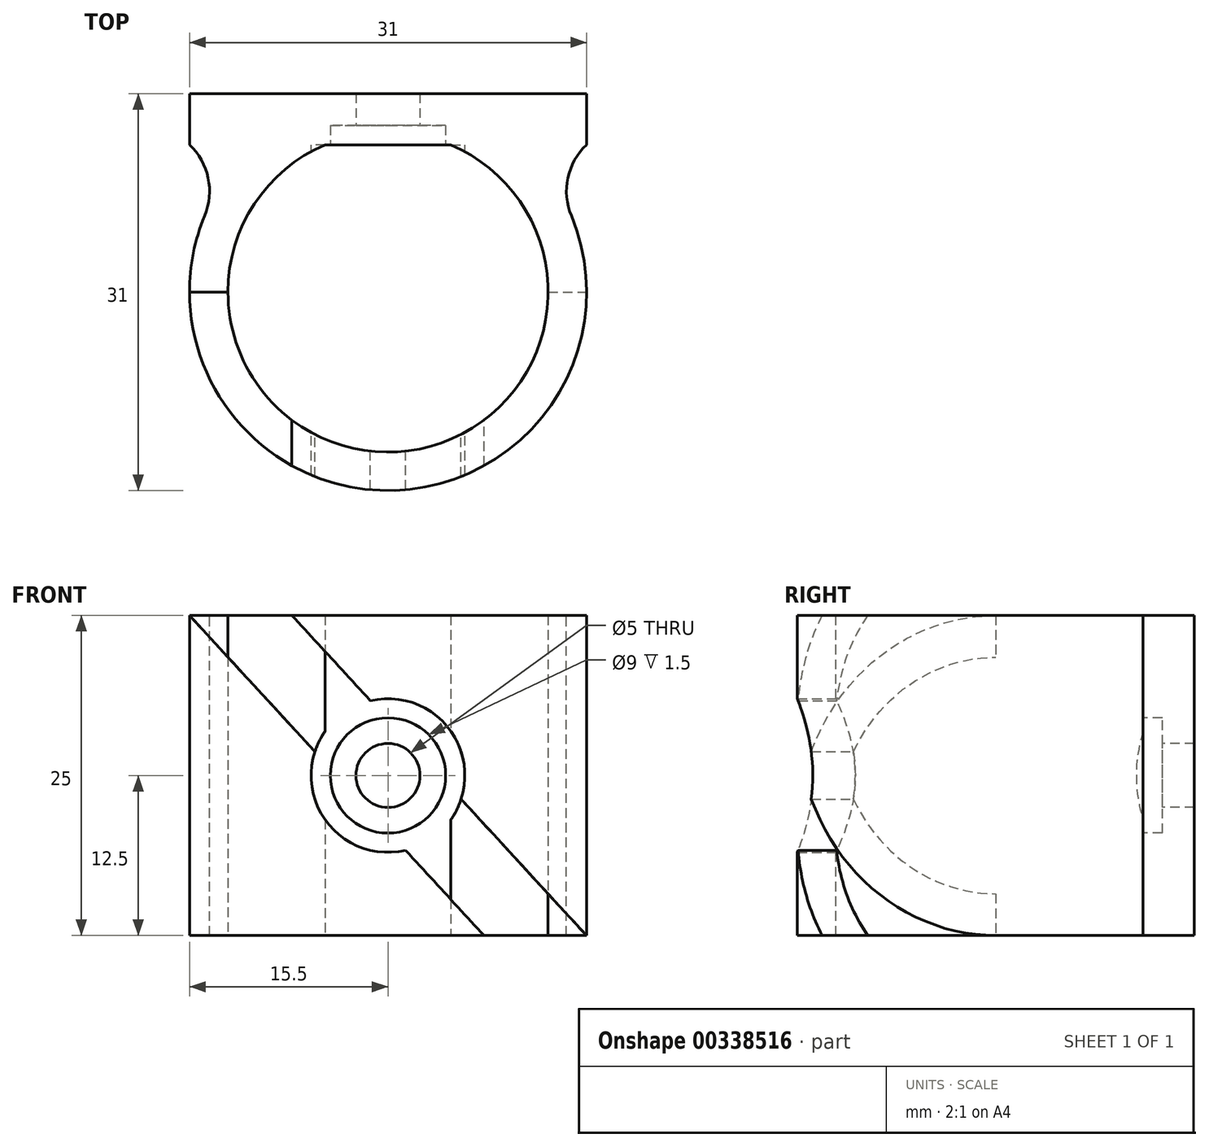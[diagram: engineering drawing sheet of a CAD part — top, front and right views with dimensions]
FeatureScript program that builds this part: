
annotation { "Feature Type Name" : "Feature", "Feature Type Description" : "" }
export const myFeature = defineFeature(function(context is Context, id is Id, definition is map)
    precondition{}
    {
        {
            var Q0;
            Q0=qCreatedBy(makeId("Top.planeOp"),FACE);
            var sketch = newSketch(context, id + "F0", { "sketchPlane" : qUnion([Q0])});
            skArc(sketch, "E0", {"start": v(-4.9, 11.5) * mm, "mid": v(0, -12.5) * mm, "end": v(4.9, 11.5) * mm});
            skArc(sketch, "E1.0", {"start": v(-10.4, 11.5) * mm, "mid": v(0, -15.5) * mm, "end": v(10.4, 11.5) * mm});
            skLineSegment(sketch, "E2.bottom", {"start": v(-15.5, 15.5) * mm, "end": v(15.5, 15.5) * mm});
            skLineSegment(sketch, "E2.top", {"start": v(-15.5, 11.5) * mm, "end": v(15.5, 11.5) * mm});
            skLineSegment(sketch, "E2.left", {"start": v(-15.5, 15.5) * mm, "end": v(-15.5, 11.5) * mm});
            skLineSegment(sketch, "E2.right", {"start": v(15.5, 15.5) * mm, "end": v(15.5, 11.5) * mm});
            skSolve(sketch);
        }
        {
            var Q0;
            {var subQ0=sQuery(id+"F0.wireOp",EDGE,"E0");Q0=makeQuery(id+"F0.imprint","IMPRINT",FACE,{"disambiguationData":[TD([[makeQuery(id+"F0.imprint","IMPRINT",EDGE,{"derivedFrom":subQ0}),-1.0]])]});}
            var Q1;
            Q1=makeQuery(id+"F0.imprint","IMPRINT",FACE,{"disambiguationData":[TD([[makeQuery(id+"F0.imprint","IMPRINT",EDGE,{"derivedFrom":sQuery(id+"F0.wireOp",EDGE,"E2.bottom")}),-1.0]])]});
            extrude(context, id + "F1", {"entities" : qUnion([Q0, Q1]), "depth" : 25 * mm, "offsetDistance" : 25 * mm});
        }
        {
            var Q0;
            {var subQ0=sQuery(id+"F0.wireOp",EDGE,"E2.top");var subQ1=sQuery(id+"F0.wireOp",EDGE,"E1.0");Q0=makeQuery(id+"F1.opExtrude","SWEPT_EDGE",EDGE,{"disambiguationData":[OSD([subQ1,subQ0]),TDD([makeQuery(id+"F0.imprint","INTERSECT",VERTEX,{"disambiguationData":[OD(1.0)],"derivedFrom":[subQ1,subQ0]})])]});}
            var Q1;
            {var subQ0=sQuery(id+"F0.wireOp",EDGE,"E2.top");var subQ1=sQuery(id+"F0.wireOp",EDGE,"E1.0");Q1=makeQuery(id+"F1.opExtrude","SWEPT_EDGE",EDGE,{"disambiguationData":[OSD([subQ1,subQ0]),TDD([makeQuery(id+"F0.imprint","INTERSECT",VERTEX,{"disambiguationData":[OD(0.0)],"derivedFrom":[subQ1,subQ0]})])]});}
            fillet(context, id + "F2", {"entities" : qUnion([Q0, Q1]), "tangentPropagation" : true, "radius" : 5 * mm, "defaultsChanged" : false, "vertexSettings" : [], "allowEdgeOverflow" : false});
        }
        {
            var Q0;
            Q0=makeQuery(id+"F1.opExtrude","SWEPT_FACE",FACE,{"disambiguationData":[OSD([sQuery(id+"F0.wireOp",EDGE,"E2.bottom")])]});
            var sketch = newSketch(context, id + "F3", { "sketchPlane" : qUnion([Q0])});
            skLineSegment(sketch, "E3", {"start": v(7.5, 25) * mm, "end": v(-15.5, 0) * mm});
            skLineSegment(sketch, "E4", {"start": v(-15.5, 0) * mm, "end": v(-7.5, 0) * mm});
            skLineSegment(sketch, "E5", {"start": v(-7.5, 0) * mm, "end": v(15.5, 25) * mm});
            skLineSegment(sketch, "E6", {"start": v(15.5, 25) * mm, "end": v(7.5, 25) * mm});
            skSolve(sketch);
        }
        {
            var Q0;
            Q0=makeQuery(id+"F3.imprint","IMPRINT",FACE,{"disambiguationData":[TD([[makeQuery(id+"F3.imprint","IMPRINT",EDGE,{"derivedFrom":sQuery(id+"F3.wireOp",EDGE,"E3")}),1.0]])]});
            var Q1;
            Q1=qCreatedBy(makeId("Front.planeOp"),FACE);
            extrude(context, id + "F4", {"entities" : qUnion([Q0]), "operationType" : NewBodyOperationType.REMOVE, "endBound" : BoundingType.THROUGH_ALL, "oppositeDirection" : true, "depth" : 42.1 * mm, "offsetDistance" : 25 * mm, "hasSecondDirection" : true, "secondDirectionBound" : SecondDirectionBoundingType.UP_TO_SURFACE, "secondDirectionOppositeDirection" : true, "secondDirectionDepth" : 15 * mm, "secondDirectionBoundEntityFace" : qUnion([Q1])});
        }
        {
            var Q0;
            {var subQ0=sQuery(id+"F0.wireOp",EDGE,"E2.top");var subQ1=sQuery(id+"F0.wireOp",EDGE,"E0");Q0=makeQuery(id+"F1.opExtrude","SWEPT_FACE",FACE,{"disambiguationData":[OSD([subQ0]),TDD([makeQuery(id+"F0.imprint","IMPRINT",EDGE,{"disambiguationData":[TD([[makeQuery(id+"F0.imprint","INTERSECT",VERTEX,{"disambiguationData":[OD(0.0)],"derivedFrom":[subQ1,subQ0]}),-1.0]])],"derivedFrom":subQ0})])]});}
            var sketch = newSketch(context, id + "F5", { "sketchPlane" : qUnion([Q0])});
            skPoint(sketch, "E7", {"position": v(0, 12.5) * mm});
            skPoint(sketch, "E7.positionSnap0", {"position": v(0, 25) * mm});
            skPoint(sketch, "E7.positionSnap1", {"position": v(4.9, 12.5) * mm});
            skSolve(sketch);
        }
        {
            var Q0;
            Q0=sQuery(id+"F5.wireOp",VERTEX,"E7");
            var Q1;
            Q1=makeQuery(id+"F1.opExtrude","SWEPT_BODY",BODY,{"disambiguationData":[OSD([sQuery(id+"F0.wireOp",EDGE,"E0"),sQuery(id+"F0.wireOp",EDGE,"E1.0"),sQuery(id+"F0.wireOp",EDGE,"E2.bottom"),sQuery(id+"F0.wireOp",EDGE,"E2.top"),sQuery(id+"F0.wireOp",EDGE,"E2.left"),sQuery(id+"F0.wireOp",EDGE,"E2.right")])]});
            hole(context, id + "F6", {"style" : HoleStyle.C_BORE, "endStyle" : HoleEndStyle.THROUGH, "holeDiameter" : 5 * mm, "cBoreDiameter" : 9 * mm, "cBoreDepth" : 1.5 * mm, "majorDiameter" : 5 * mm, "tappedDepth" : 12 * mm, "tapClearance" : 3, "locations" : qUnion([Q0]), "scope" : qUnion([Q1])});
        }
        {
            var Q0;
            Q0=sQuery(id+"F5.wireOp",VERTEX,"E7");
            var Q1;
            Q1=makeQuery(id+"F1.opExtrude","SWEPT_BODY",BODY,{"disambiguationData":[OSD([sQuery(id+"F0.wireOp",EDGE,"E0"),sQuery(id+"F0.wireOp",EDGE,"E1.0"),sQuery(id+"F0.wireOp",EDGE,"E2.bottom"),sQuery(id+"F0.wireOp",EDGE,"E2.top"),sQuery(id+"F0.wireOp",EDGE,"E2.left"),sQuery(id+"F0.wireOp",EDGE,"E2.right")])]});
            hole(context, id + "F7", {"style" : HoleStyle.SIMPLE, "endStyle" : HoleEndStyle.THROUGH, "oppositeDirection" : true, "holeDiameter" : 12 * mm, "majorDiameter" : 5 * mm, "tappedDepth" : 12 * mm, "tapClearance" : 3, "locations" : qUnion([Q0]), "scope" : qUnion([Q1])});
        }
    });
